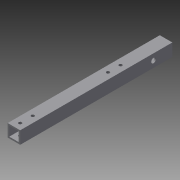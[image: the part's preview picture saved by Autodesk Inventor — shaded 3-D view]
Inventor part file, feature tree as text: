
AUTODESK INVENTOR PART (.ipt)
format: ipt  version: 2015 SP1 (Build 190203100, 203)  size: 111,616 bytes
history: native  units: in
note: dims shown in document units (in); Inventor stores cm internally (conversion verified against a paired STEP export)
features: sketch x4, extrude x2, hole x2
ambient origin geometry x8: Origin, YZ Plane, XZ Plane, XY Plane, X Axis, Y Axis, Z Axis, Center Point
bodies: Solid1 (feature_tree)
feature tree (8):
  extrude  "Extrusion1"  Depth=1.0in
  hole  "Hole1"  [1 undecoded]
  hole  "Hole2"  [1 undecoded]
  extrude  "Extrusion2"  Depth=1.0in
  sketch  "Sketch1"  dims[d0=1.0in d1=1.0in]
  sketch  "Sketch2"  dims[d2=0.75in d3=0.75in]
  sketch  "Sketch3"  dims[d4=0.125in d5=0.125in]
  sketch  "Sketch4"  dims[d6=12.125in d7=0.0in d8=0.5in d9=0.5in d11=0.5in d16=0.5in d17=0.5in d18=0.25in d19=0.75in d20=0.375in d21=0.25in d22=0.5635in d23=1.0in d24=0.8108in d25=1.5in d26=0.5in d27=0.375in d28=0.75in d29=0.375in d30=0.25in d31=0.5635in d32=1.0in d33=0.8108in d34=6.0in d35=1.0in d36=1.0in d37=0.5in d38=0.5in d39=0.0in]
note: 2 required parameter values undecoded (feature->parameter linkage not recoverable at this tier; creation-order binding heuristic only, values carry confidence <= 0.55)
